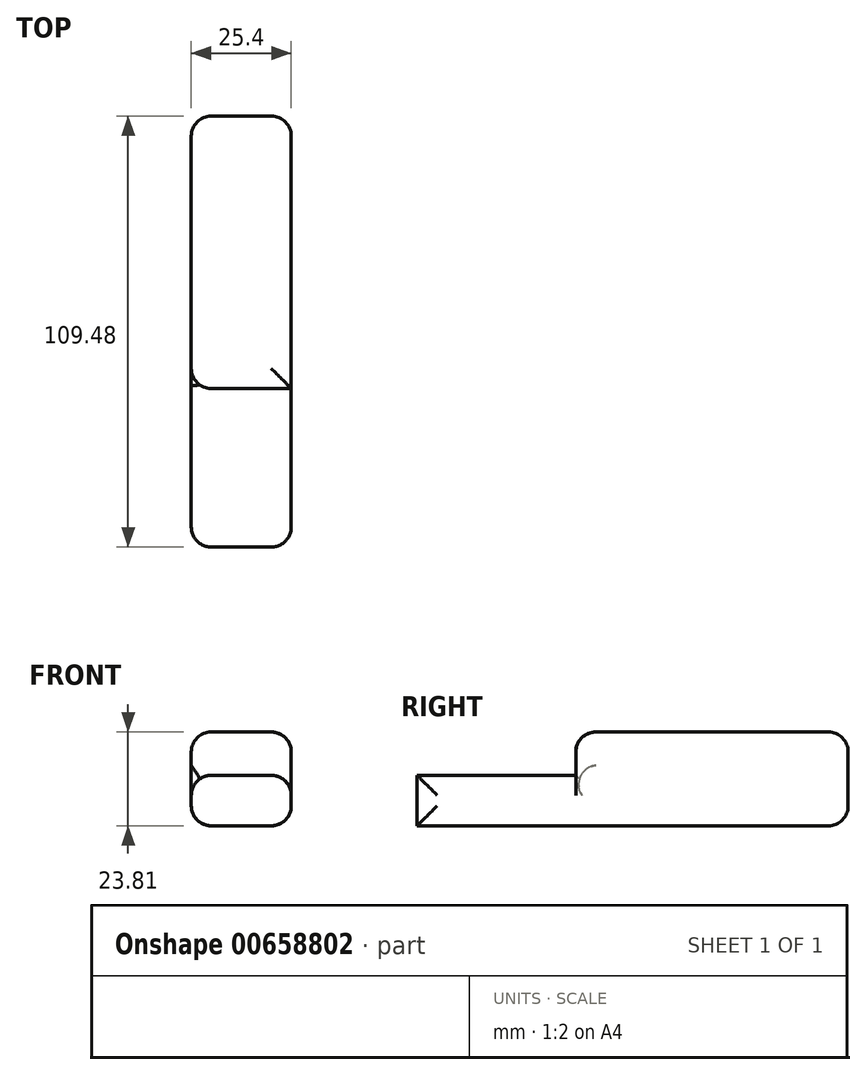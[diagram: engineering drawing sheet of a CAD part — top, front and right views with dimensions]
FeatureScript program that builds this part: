
annotation { "Feature Type Name" : "Feature", "Feature Type Description" : "" }
export const myFeature = defineFeature(function(context is Context, id is Id, definition is map)
    precondition{}
    {
        {
            var Q0;
            Q0=qCreatedBy(makeId("Right.planeOp"),FACE);
            var sketch = newSketch(context, id + "F0", { "sketchPlane" : qUnion([Q0])});
            skLineSegment(sketch, "E0", {"start": v(-38.66, 33) * mm, "end": v(1.63, 33) * mm});
            skLineSegment(sketch, "E1", {"start": v(1.63, 33) * mm, "end": v(1.63, 44) * mm});
            skLineSegment(sketch, "E2", {"start": v(1.63, 44) * mm, "end": v(55.36, 44) * mm});
            skLineSegment(sketch, "E3", {"start": v(-38.66, 33) * mm, "end": v(-38.66, 20.19) * mm});
            skLineSegment(sketch, "E4", {"start": v(-38.66, 20.19) * mm, "end": v(70.82, 20.19) * mm});
            skLineSegment(sketch, "E5", {"start": v(70.82, 20.19) * mm, "end": v(70.82, 44) * mm});
            skLineSegment(sketch, "E6", {"start": v(55.36, 44) * mm, "end": v(70.82, 44) * mm});
            skSolve(sketch);
        }
        {
            var Q0;
            Q0 = qSketchRegion(id + "F0", true);
            extrude(context, id + "F1", {"entities" : qUnion([Q0]), "depth" : 25.4 * mm, "offsetDistance" : 25.4 * mm});
        }
        {
            var Q0;
            Q0=makeQuery(id+"F1.opExtrude","CAP_EDGE",EDGE,{"disambiguationData":[OSD([sQuery(id+"F0.wireOp",EDGE,"E2"),sQuery(id+"F0.wireOp",EDGE,"E6")])],"isStart":false});
            var Q1;
            Q1=makeQuery(id+"F1.opExtrude","CAP_EDGE",EDGE,{"disambiguationData":[OSD([sQuery(id+"F0.wireOp",EDGE,"E0")])],"isStart":false});
            var Q2;
            Q2=makeQuery(id+"F1.opExtrude","SWEPT_EDGE",EDGE,{"disambiguationData":[OSD([sQuery(id+"F0.wireOp",EDGE,"E1"),sQuery(id+"F0.wireOp",EDGE,"E2")])]});
            var Q3;
            Q3=makeQuery(id+"F1.opExtrude","CAP_EDGE",EDGE,{"disambiguationData":[OSD([sQuery(id+"F0.wireOp",EDGE,"E0")])],"isStart":true});
            var Q4;
            Q4=makeQuery(id+"F1.opExtrude","CAP_EDGE",EDGE,{"disambiguationData":[OSD([sQuery(id+"F0.wireOp",EDGE,"E3")])],"isStart":false});
            var Q5;
            Q5=makeQuery(id+"F1.opExtrude","CAP_EDGE",EDGE,{"disambiguationData":[OSD([sQuery(id+"F0.wireOp",EDGE,"E3")])],"isStart":true});
            var Q6;
            Q6=makeQuery(id+"F1.opExtrude","CAP_EDGE",EDGE,{"disambiguationData":[OSD([sQuery(id+"F0.wireOp",EDGE,"E4")])],"isStart":false});
            var Q7;
            Q7=makeQuery(id+"F1.opExtrude","CAP_FACE",FACE,{"disambiguationData":[OSD([sQuery(id+"F0.wireOp",EDGE,"E0"),sQuery(id+"F0.wireOp",EDGE,"E1"),sQuery(id+"F0.wireOp",EDGE,"E2"),sQuery(id+"F0.wireOp",EDGE,"E3"),sQuery(id+"F0.wireOp",EDGE,"E4"),sQuery(id+"F0.wireOp",EDGE,"E5"),sQuery(id+"F0.wireOp",EDGE,"E6")])],"isStart":true});
            var Q8;
            Q8=makeQuery(id+"F1.opExtrude","SWEPT_FACE",FACE,{"disambiguationData":[OSD([sQuery(id+"F0.wireOp",EDGE,"E5")])]});
            fillet(context, id + "F2", {"entities" : qUnion([Q0, Q1, Q2, Q3, Q4, Q5, Q6, Q7, Q8]), "radius" : 5.08 * mm, "tangentPropagation" : true, "allowEdgeOverflow" : false});
        }
        {
            var Q0;
            Q0=makeQuery(id+"F1.opExtrude","CAP_FACE",FACE,{"disambiguationData":[OSD([sQuery(id+"F0.wireOp",EDGE,"E0"),sQuery(id+"F0.wireOp",EDGE,"E1"),sQuery(id+"F0.wireOp",EDGE,"E2"),sQuery(id+"F0.wireOp",EDGE,"E3"),sQuery(id+"F0.wireOp",EDGE,"E4"),sQuery(id+"F0.wireOp",EDGE,"E5"),sQuery(id+"F0.wireOp",EDGE,"E6")])],"isStart":false});
            var sketch = newSketch(context, id + "F3", { "sketchPlane" : qUnion([Q0])});
            skCircle(sketch, "E7", {"center": v(56.6, 32.44) * mm, "radius": 6.16 * mm});
            skCircle(sketch, "E8", {"center": v(7.3, 30.64) * mm, "radius": 4.94 * mm});
            skLineSegment(sketch, "E9.bottom", {"start": v(57.06, 29.7) * mm, "end": v(56.6, 29.7) * mm});
            skLineSegment(sketch, "E9.top", {"start": v(57.06, 32.44) * mm, "end": v(56.6, 32.44) * mm});
            skLineSegment(sketch, "E9.left", {"start": v(57.06, 29.7) * mm, "end": v(57.06, 32.44) * mm});
            skLineSegment(sketch, "E9.right", {"start": v(56.6, 29.7) * mm, "end": v(56.6, 32.44) * mm});
            skSolve(sketch);
        }
        {
            var Q0;
            Q0 = qSketchRegion(id + "F3", true);
            extrude(context, id + "F4", {"entities" : qUnion([Q0]), "operationType" : NewBodyOperationType.ADD, "oppositeDirection" : true, "depth" : 25.4 * mm, "offsetDistance" : 25.4 * mm});
        }
    });
